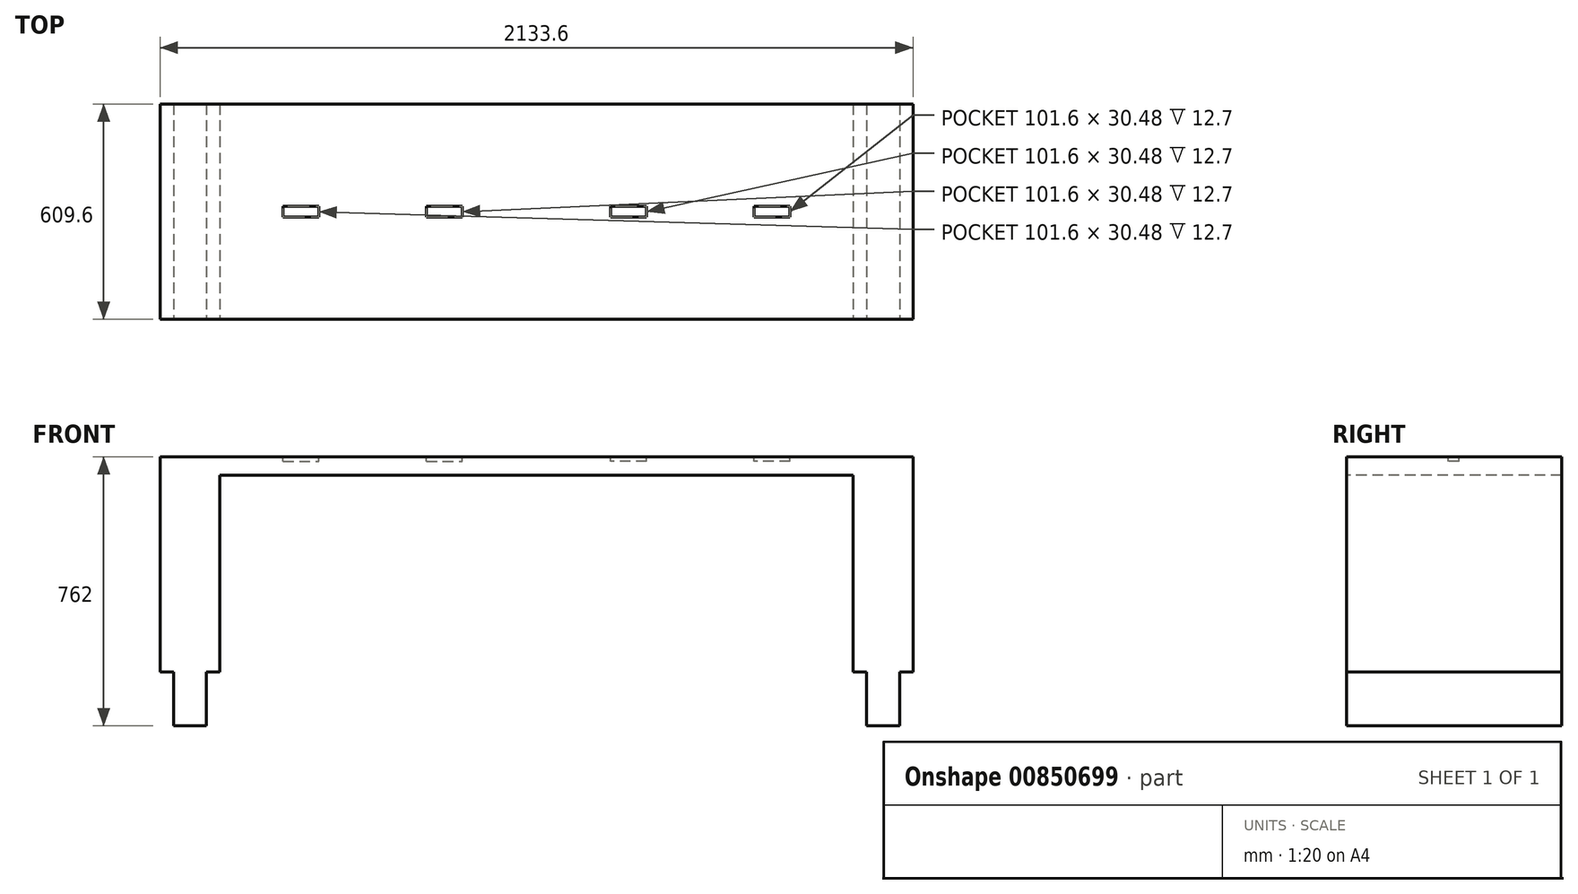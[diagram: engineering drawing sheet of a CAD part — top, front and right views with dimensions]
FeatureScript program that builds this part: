
annotation { "Feature Type Name" : "Feature", "Feature Type Description" : "" }
export const myFeature = defineFeature(function(context is Context, id is Id, definition is map)
    precondition{}
    {
        {
            var Q0;
            Q0=qCreatedBy(makeId("Top.planeOp"),FACE);
            var sketch = newSketch(context, id + "F0", { "sketchPlane" : qUnion([Q0])});
            skLineSegment(sketch, "E0.bottom", {"start": v(-1082.41, -163.07) * mm, "end": v(1051.19, -163.07) * mm});
            skLineSegment(sketch, "E0.top", {"start": v(-1082.41, -772.67) * mm, "end": v(1051.19, -772.67) * mm});
            skLineSegment(sketch, "E0.left", {"start": v(-1082.41, -163.07) * mm, "end": v(-1082.41, -772.67) * mm});
            skLineSegment(sketch, "E0.right", {"start": v(1051.19, -163.07) * mm, "end": v(1051.19, -772.67) * mm});
            skSolve(sketch);
        }
        {
            var Q0;
            Q0=makeQuery(id+"F0.imprint","IMPRINT",FACE,{"disambiguationData":[TD([[makeQuery(id+"F0.imprint","IMPRINT",EDGE,{"derivedFrom":sQuery(id+"F0.wireOp",EDGE,"E0.bottom")}),-1.0]])]});
            extrude(context, id + "F1", {"entities" : qUnion([Q0]), "depth" : 762 * mm, "offsetDistance" : 25.4 * mm});
        }
        {
            var Q0;
            Q0=makeQuery(id+"F1.opExtrude","SWEPT_FACE",FACE,{"disambiguationData":[OSD([sQuery(id+"F0.wireOp",EDGE,"E0.top")])]});
            var sketch = newSketch(context, id + "F2", { "sketchPlane" : qUnion([Q0])});
            skLineSegment(sketch, "E1", {"start": v(-1082.41, 152.4) * mm, "end": v(-1044.31, 152.4) * mm});
            skLineSegment(sketch, "E2", {"start": v(-1044.31, 152.4) * mm, "end": v(-1044.31, 0) * mm});
            skLineSegment(sketch, "E3", {"start": v(-1044.31, 0) * mm, "end": v(-950.73, 0) * mm});
            skLineSegment(sketch, "E4", {"start": v(-950.73, 0) * mm, "end": v(-950.73, 152.4) * mm});
            skLineSegment(sketch, "E5", {"start": v(-950.73, 152.4) * mm, "end": v(-912.63, 152.4) * mm});
            skLineSegment(sketch, "E6", {"start": v(-912.63, 152.4) * mm, "end": v(-912.63, 710.4) * mm});
            skLineSegment(sketch, "E7", {"start": v(-912.63, 710.4) * mm, "end": v(924.4, 710.4) * mm});
            skLineSegment(sketch, "E8", {"start": v(1013.09, 0) * mm, "end": v(1013.09, 152.4) * mm});
            skLineSegment(sketch, "E9", {"start": v(1013.09, 152.4) * mm, "end": v(1051.19, 152.4) * mm});
            skLineSegment(sketch, "E10", {"start": v(-1082.41, 152.4) * mm, "end": v(-1082.41, 0) * mm});
            skLineSegment(sketch, "E11", {"start": v(-1082.41, 0) * mm, "end": v(-1044.31, 0) * mm});
            skLineSegment(sketch, "E12", {"start": v(-15.61, 762) * mm, "end": v(-15.61, 0) * mm});
            skLineSegment(sketch, "E13.MirrorCS", {"start": v(1051.19, 152.4) * mm, "end": v(1013.09, 152.4) * mm});
            skLineSegment(sketch, "E14.MirrorCS", {"start": v(919.5, 0) * mm, "end": v(919.5, 152.4) * mm});
            skLineSegment(sketch, "E15.MirrorCS", {"start": v(919.5, 152.4) * mm, "end": v(881.4, 152.4) * mm});
            skLineSegment(sketch, "E16.MirrorCS", {"start": v(881.4, 152.4) * mm, "end": v(881.4, 710.4) * mm});
            skLineSegment(sketch, "E17.MirrorCS", {"start": v(881.4, 710.4) * mm, "end": v(-955.62, 710.4) * mm});
            skLineSegment(sketch, "E18", {"start": v(-950.73, 0) * mm, "end": v(919.5, 0) * mm});
            skSolve(sketch);
        }
        {
            var Q0;
            {var subQ6=sQuery(id+"F2.wireOp",EDGE,"E4");Q0=makeQuery(id+"F2.imprint","IMPRINT",FACE,{"disambiguationData":[TD([[makeQuery(id+"F2.imprint","IMPRINT",EDGE,{"derivedFrom":subQ6}),-1.0]])]});}
            var Q1;
            {var subQ1=sQuery(id+"F2.wireOp",EDGE,"E14.MirrorCS");Q1=makeQuery(id+"F2.imprint","IMPRINT",FACE,{"disambiguationData":[TD([[makeQuery(id+"F2.imprint","IMPRINT",EDGE,{"derivedFrom":subQ1}),1.0]])]});}
            extrude(context, id + "F3", {"entities" : qUnion([Q0, Q1]), "operationType" : NewBodyOperationType.REMOVE, "oppositeDirection" : true, "depth" : 15240 * mm, "offsetDistance" : 25.4 * mm});
        }
        {
            var Q0;
            Q0 = qSketchRegion(id + "F2", true);
            extrude(context, id + "F4", {"entities" : qUnion([Q0]), "operationType" : NewBodyOperationType.REMOVE, "oppositeDirection" : true, "depth" : 1270 * mm, "offsetDistance" : 25.4 * mm});
        }
        {
            var Q0;
            Q0=makeQuery(id+"F2.imprint","IMPRINT",FACE,{"disambiguationData":[TD([[makeQuery(id+"F2.imprint","IMPRINT",EDGE,{"derivedFrom":sQuery(id+"F2.wireOp",EDGE,"E1")}),-1.0]])]});
            var Q1;
            {var subQ0=sQuery(id+"F2.wireOp",EDGE,"E8");Q1=makeQuery(id+"F2.imprint","IMPRINT",FACE,{"disambiguationData":[TD([[makeQuery(id+"F2.imprint","IMPRINT",EDGE,{"derivedFrom":subQ0}),-1.0]])]});}
            extrude(context, id + "F5", {"entities" : qUnion([Q0, Q1]), "operationType" : NewBodyOperationType.REMOVE, "oppositeDirection" : true, "depth" : 1270 * mm, "offsetDistance" : 25.4 * mm});
        }
        {
            var Q0;
            Q0=makeQuery(id+"F1.opExtrude","CAP_FACE",FACE,{"disambiguationData":[OSD([sQuery(id+"F0.wireOp",EDGE,"E0.bottom"),sQuery(id+"F0.wireOp",EDGE,"E0.top"),sQuery(id+"F0.wireOp",EDGE,"E0.left"),sQuery(id+"F0.wireOp",EDGE,"E0.right")])],"isStart":false});
            var sketch = newSketch(context, id + "F6", { "sketchPlane" : qUnion([Q0])});
            skLineSegment(sketch, "E19", {"start": v(-15.61, -163.07) * mm, "end": v(-15.61, -772.67) * mm});
            skLineSegment(sketch, "E20", {"start": v(-1082.41, -467.87) * mm, "end": v(1051.19, -467.87) * mm});
            skLineSegment(sketch, "E21.bottom", {"start": v(-733.7, -453.2) * mm, "end": v(-632.1, -453.2) * mm});
            skLineSegment(sketch, "E21.top", {"start": v(-733.7, -483.67) * mm, "end": v(-632.1, -483.67) * mm});
            skLineSegment(sketch, "E21.left", {"start": v(-733.7, -453.2) * mm, "end": v(-733.7, -483.67) * mm});
            skLineSegment(sketch, "E21.right", {"start": v(-632.1, -453.2) * mm, "end": v(-632.1, -483.67) * mm});
            skLineSegment(sketch, "E22", {"start": v(-327.25, -467.87) * mm, "end": v(-632.05, -467.87) * mm, "construction": true});
            skLineSegment(sketch, "E23.bottom", {"start": v(-327.48, -453) * mm, "end": v(-225.88, -453) * mm});
            skLineSegment(sketch, "E23.top", {"start": v(-327.48, -483.49) * mm, "end": v(-225.88, -483.49) * mm});
            skLineSegment(sketch, "E23.left", {"start": v(-327.48, -453) * mm, "end": v(-327.48, -483.49) * mm});
            skLineSegment(sketch, "E23.right", {"start": v(-225.88, -453) * mm, "end": v(-225.88, -483.49) * mm});
            skLineSegment(sketch, "E24.MirrorCS", {"start": v(296.25, -453) * mm, "end": v(194.65, -453) * mm});
            skLineSegment(sketch, "E25.MirrorCS", {"start": v(296.25, -483.49) * mm, "end": v(194.65, -483.49) * mm});
            skLineSegment(sketch, "E26.MirrorCS", {"start": v(194.65, -453) * mm, "end": v(194.65, -483.49) * mm});
            skLineSegment(sketch, "E27.MirrorCS", {"start": v(296.25, -453) * mm, "end": v(296.25, -483.49) * mm});
            skLineSegment(sketch, "E28.MirrorCS", {"start": v(600.87, -453.2) * mm, "end": v(600.87, -483.67) * mm});
            skLineSegment(sketch, "E29.MirrorCS", {"start": v(702.47, -483.67) * mm, "end": v(600.87, -483.67) * mm});
            skLineSegment(sketch, "E30.MirrorCS", {"start": v(702.47, -453.2) * mm, "end": v(600.87, -453.2) * mm});
            skLineSegment(sketch, "E31.MirrorCS", {"start": v(702.47, -453.2) * mm, "end": v(702.47, -483.67) * mm});
            skSolve(sketch);
        }
        {
            var Q0;
            {var subQ5=sQuery(id+"F6.wireOp",EDGE,"E21.bottom");Q0=makeQuery(id+"F6.imprint","IMPRINT",FACE,{"disambiguationData":[TD([[makeQuery(id+"F6.imprint","IMPRINT",EDGE,{"derivedFrom":subQ5}),-1.0]])]});}
            var Q1;
            {var subQ5=sQuery(id+"F6.wireOp",EDGE,"E21.top");Q1=makeQuery(id+"F6.imprint","IMPRINT",FACE,{"disambiguationData":[TD([[makeQuery(id+"F6.imprint","IMPRINT",EDGE,{"derivedFrom":subQ5}),1.0]])]});}
            var Q2;
            {var subQ5=sQuery(id+"F6.wireOp",EDGE,"E23.top");Q2=makeQuery(id+"F6.imprint","IMPRINT",FACE,{"disambiguationData":[TD([[makeQuery(id+"F6.imprint","IMPRINT",EDGE,{"derivedFrom":subQ5}),1.0]])]});}
            var Q3;
            {var subQ5=sQuery(id+"F6.wireOp",EDGE,"E23.bottom");Q3=makeQuery(id+"F6.imprint","IMPRINT",FACE,{"disambiguationData":[TD([[makeQuery(id+"F6.imprint","IMPRINT",EDGE,{"derivedFrom":subQ5}),-1.0]])]});}
            var Q4;
            {var subQ5=sQuery(id+"F6.wireOp",EDGE,"E25.MirrorCS");Q4=makeQuery(id+"F6.imprint","IMPRINT",FACE,{"disambiguationData":[TD([[makeQuery(id+"F6.imprint","IMPRINT",EDGE,{"derivedFrom":subQ5}),-1.0]])]});}
            var Q5;
            {var subQ5=sQuery(id+"F6.wireOp",EDGE,"E24.MirrorCS");Q5=makeQuery(id+"F6.imprint","IMPRINT",FACE,{"disambiguationData":[TD([[makeQuery(id+"F6.imprint","IMPRINT",EDGE,{"derivedFrom":subQ5}),1.0]])]});}
            var Q6;
            {var subQ5=sQuery(id+"F6.wireOp",EDGE,"E29.MirrorCS");Q6=makeQuery(id+"F6.imprint","IMPRINT",FACE,{"disambiguationData":[TD([[makeQuery(id+"F6.imprint","IMPRINT",EDGE,{"derivedFrom":subQ5}),-1.0]])]});}
            var Q7;
            {var subQ5=sQuery(id+"F6.wireOp",EDGE,"E30.MirrorCS");Q7=makeQuery(id+"F6.imprint","IMPRINT",FACE,{"disambiguationData":[TD([[makeQuery(id+"F6.imprint","IMPRINT",EDGE,{"derivedFrom":subQ5}),1.0]])]});}
            extrude(context, id + "F7", {"entities" : qUnion([Q0, Q1, Q2, Q3, Q4, Q5, Q6, Q7]), "operationType" : NewBodyOperationType.REMOVE, "oppositeDirection" : true, "depth" : 12.7 * mm, "offsetDistance" : 25.4 * mm});
        }
    });
